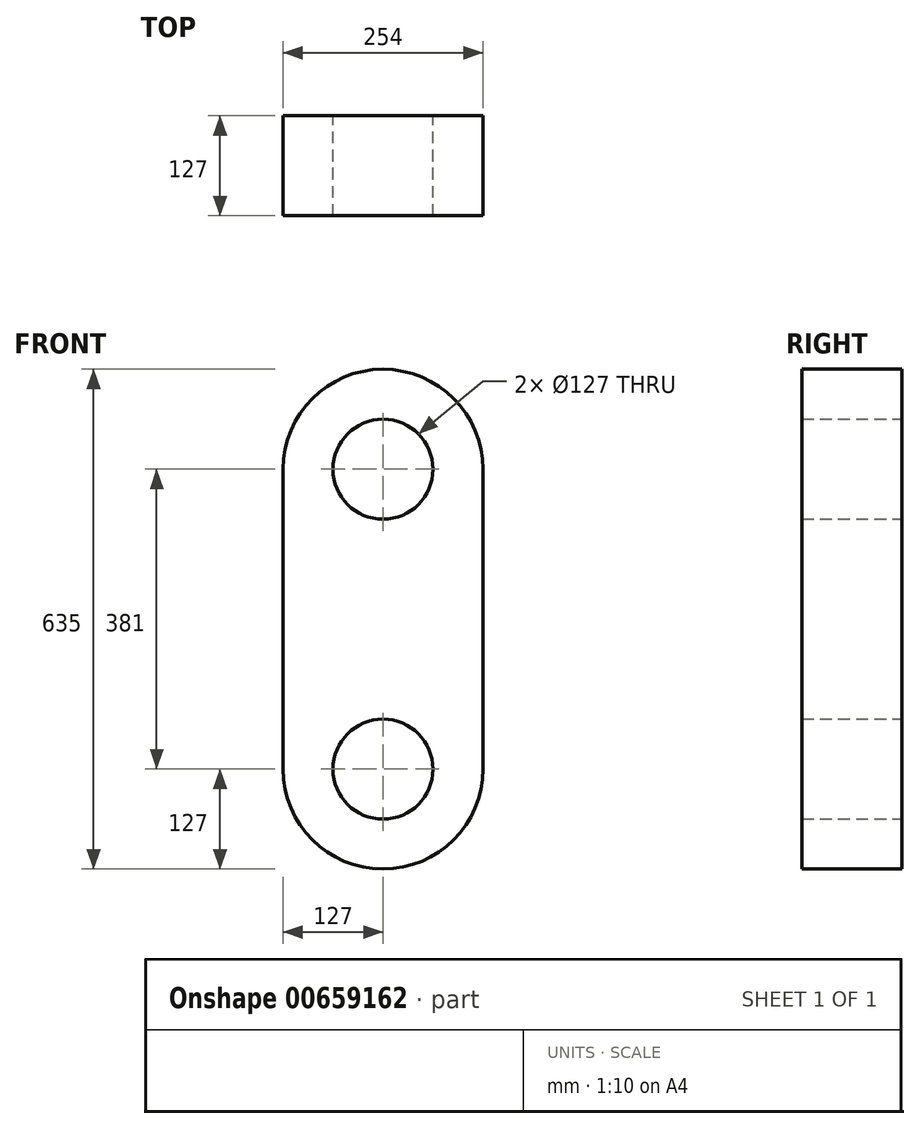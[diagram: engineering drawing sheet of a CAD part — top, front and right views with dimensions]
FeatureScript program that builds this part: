
annotation { "Feature Type Name" : "Feature", "Feature Type Description" : "" }
export const myFeature = defineFeature(function(context is Context, id is Id, definition is map)
    precondition{}
    {
        {
            var Q0;
            Q0=qCreatedBy(makeId("Front.planeOp"),FACE);
            var sketch = newSketch(context, id + "F0", { "sketchPlane" : qUnion([Q0])});
            skLineSegment(sketch, "E0.left", {"start": v(-127, 190.5) * mm, "end": v(-127, -190.5) * mm});
            skLineSegment(sketch, "E0.right", {"start": v(127, 190.5) * mm, "end": v(127, -190.5) * mm});
            skPoint(sketch, "E0.middle", {"position": v(0, 0) * mm});
            skArc(sketch, "E1", {"start": v(127, 190.5) * mm, "mid": v(0, 317.5) * mm, "end": v(-127, 190.5) * mm});
            skCircle(sketch, "E2", {"center": v(0, 190.5) * mm, "radius": 63.5 * mm});
            skArc(sketch, "E3", {"start": v(-127, -190.5) * mm, "mid": v(0, -317.5) * mm, "end": v(127, -190.5) * mm});
            skCircle(sketch, "E4", {"center": v(0, -190.5) * mm, "radius": 63.5 * mm});
            skSolve(sketch);
        }
        {
            var Q0;
            Q0=makeQuery(id+"F0.imprint","IMPRINT",FACE,{"disambiguationData":[TD([[makeQuery(id+"F0.imprint","IMPRINT",EDGE,{"derivedFrom":sQuery(id+"F0.wireOp",EDGE,"E0.left")}),1.0]])]});
            extrude(context, id + "F1", {"entities" : qUnion([Q0]), "depth" : 127 * mm, "offsetDistance" : 25.4 * mm});
        }
    });
